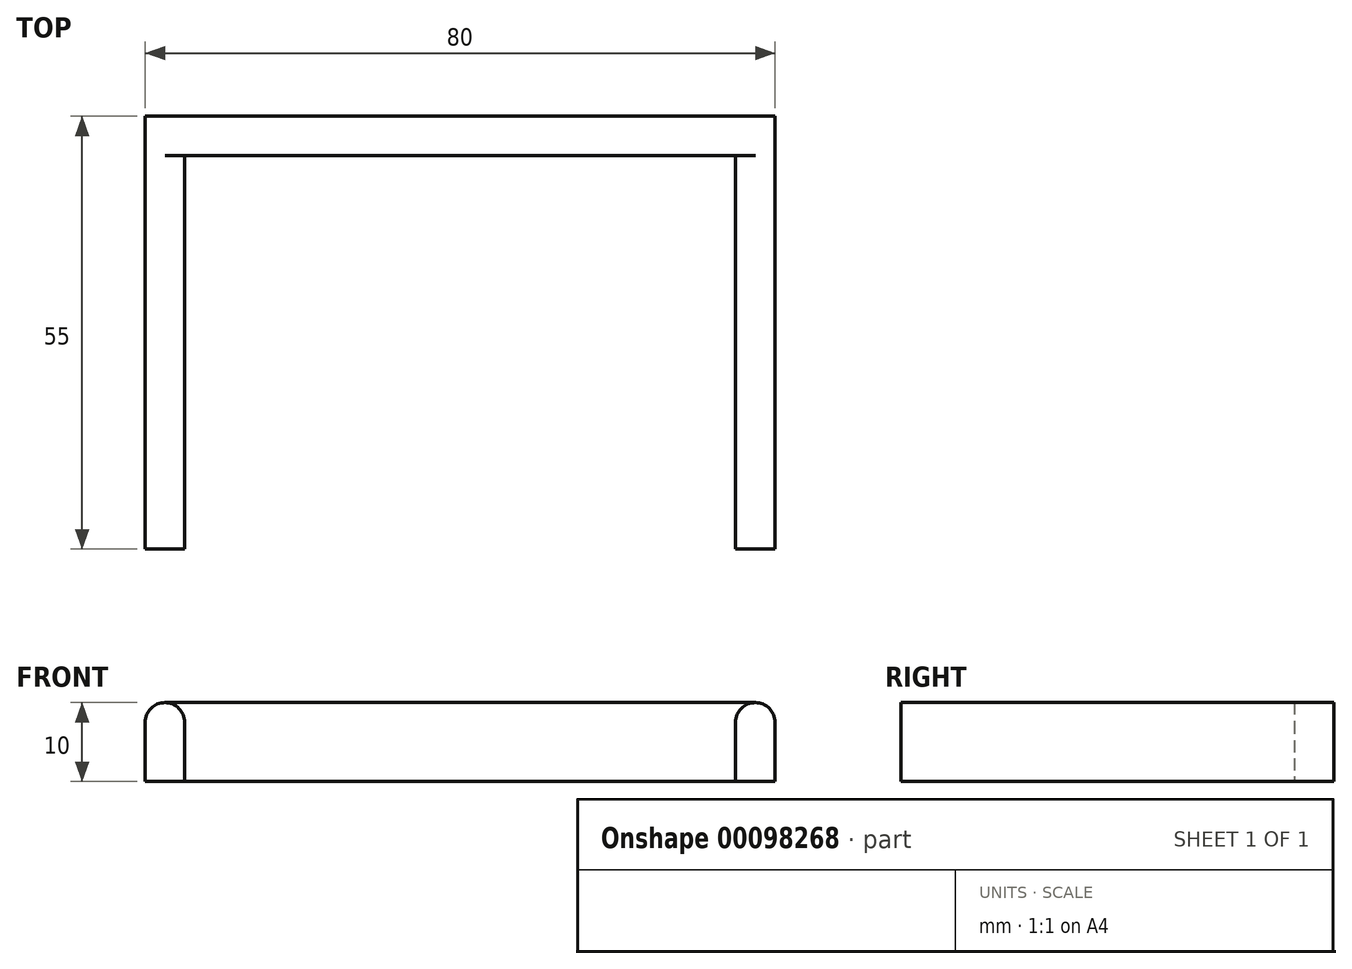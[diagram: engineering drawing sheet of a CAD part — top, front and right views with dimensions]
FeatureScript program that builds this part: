
annotation { "Feature Type Name" : "Feature", "Feature Type Description" : "" }
export const myFeature = defineFeature(function(context is Context, id is Id, definition is map)
    precondition{}
    {
        {
            var Q0;
            Q0=qCreatedBy(makeId("Top.planeOp"),FACE);
            var sketch = newSketch(context, id + "F0", { "sketchPlane" : qUnion([Q0])});
            skLineSegment(sketch, "E0", {"start": v(-44.69, -29.23) * mm, "end": v(-44.69, 25.77) * mm});
            skLineSegment(sketch, "E1", {"start": v(-44.69, 25.77) * mm, "end": v(35.31, 25.77) * mm});
            skLineSegment(sketch, "E2", {"start": v(35.31, 25.77) * mm, "end": v(35.31, -29.23) * mm});
            skLineSegment(sketch, "E3", {"start": v(35.31, -29.23) * mm, "end": v(30.31, -29.23) * mm});
            skLineSegment(sketch, "E4", {"start": v(30.31, -29.23) * mm, "end": v(30.31, 20.77) * mm});
            skLineSegment(sketch, "E5", {"start": v(30.31, 20.77) * mm, "end": v(-39.69, 20.77) * mm});
            skLineSegment(sketch, "E6", {"start": v(-39.69, 20.77) * mm, "end": v(-39.69, -29.23) * mm});
            skLineSegment(sketch, "E7", {"start": v(-39.69, -29.23) * mm, "end": v(-44.69, -29.23) * mm});
            skSolve(sketch);
        }
        {
            var Q0;
            Q0=makeQuery(id+"F0.imprint","IMPRINT",FACE,{"disambiguationData":[TD([[makeQuery(id+"F0.imprint","IMPRINT",EDGE,{"derivedFrom":sQuery(id+"F0.wireOp",EDGE,"E0")}),-1.0]])]});
            extrude(context, id + "F1", {"entities" : qUnion([Q0]), "depth" : 10 * mm});
        }
        {
            var Q0;
            Q0=makeQuery(id+"F1.opExtrude","CAP_EDGE",EDGE,{"disambiguationData":[OSD([sQuery(id+"F0.wireOp",EDGE,"E0")])],"isStart":false});
            var Q1;
            Q1=makeQuery(id+"F1.opExtrude","CAP_EDGE",EDGE,{"disambiguationData":[OSD([sQuery(id+"F0.wireOp",EDGE,"E6")])],"isStart":false});
            var Q2;
            Q2=makeQuery(id+"F1.opExtrude","CAP_EDGE",EDGE,{"disambiguationData":[OSD([sQuery(id+"F0.wireOp",EDGE,"E4")])],"isStart":false});
            var Q3;
            Q3=makeQuery(id+"F1.opExtrude","CAP_EDGE",EDGE,{"disambiguationData":[OSD([sQuery(id+"F0.wireOp",EDGE,"E2")])],"isStart":false});
            fillet(context, id + "F2", {"entities" : qUnion([Q0, Q1, Q2, Q3]), "radius" : 2.5 * mm, "tangentPropagation" : true, "allowEdgeOverflow" : false});
        }
    });
